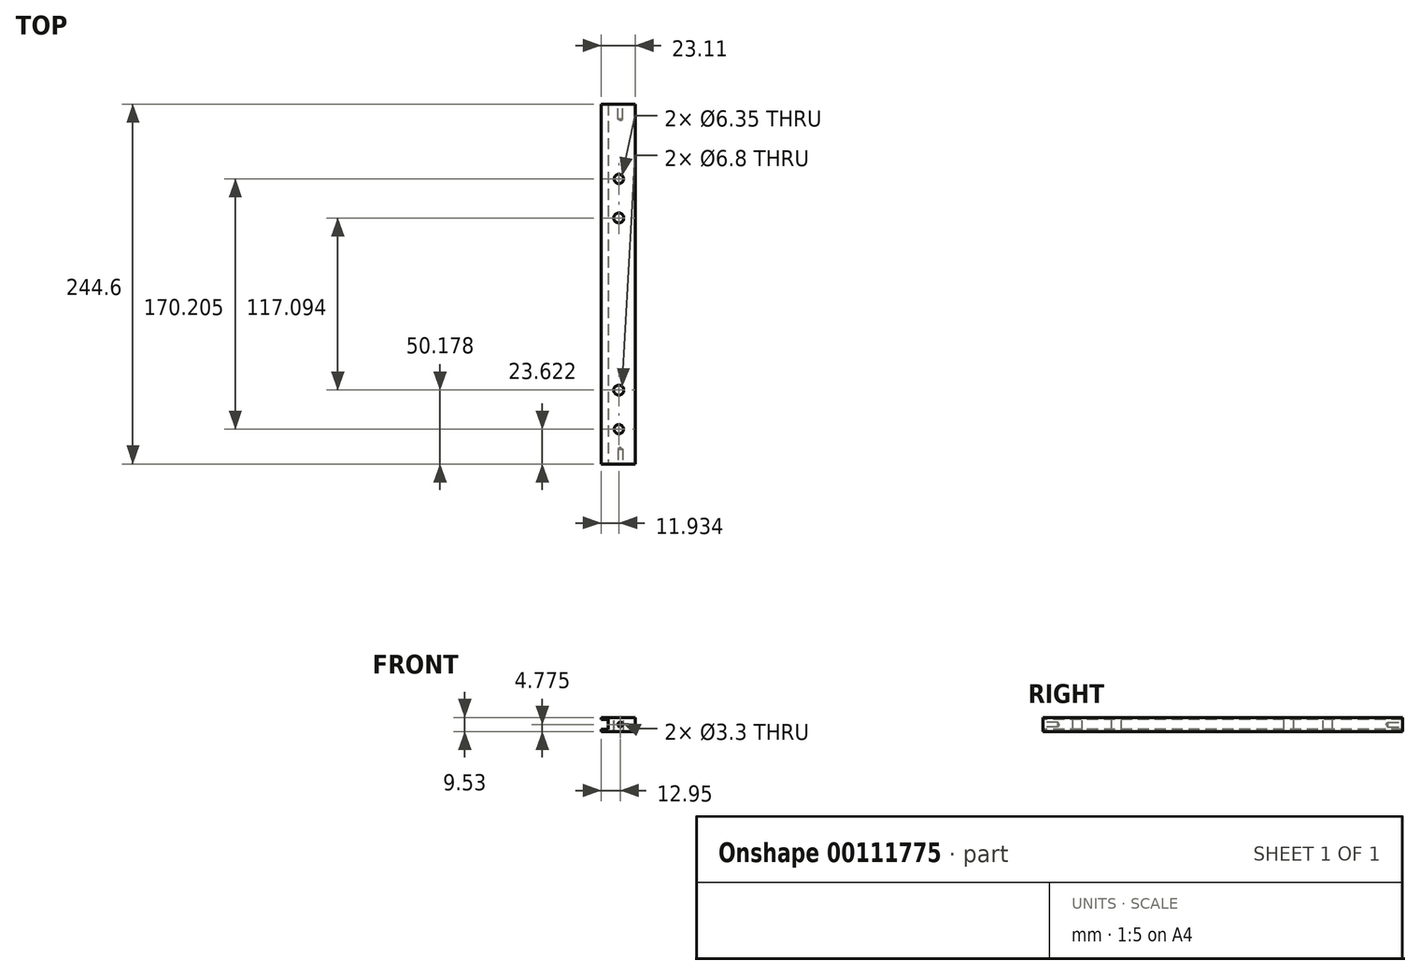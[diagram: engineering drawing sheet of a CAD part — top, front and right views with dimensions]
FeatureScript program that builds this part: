
annotation { "Feature Type Name" : "Feature", "Feature Type Description" : "" }
export const myFeature = defineFeature(function(context is Context, id is Id, definition is map)
    precondition{}
    {
        {
            var Q0;
            Q0=qCreatedBy(makeId("Top.planeOp"),FACE);
            var sketch = newSketch(context, id + "F0", { "sketchPlane" : qUnion([Q0])});
            skLineSegment(sketch, "E0.bottom", {"start": v(0, 0) * mm, "end": v(-23.11, 0) * mm});
            skLineSegment(sketch, "E0.top", {"start": v(0, 244.6) * mm, "end": v(-23.11, 244.6) * mm});
            skLineSegment(sketch, "E0.left", {"start": v(0, 0) * mm, "end": v(0, 244.6) * mm});
            skLineSegment(sketch, "E0.right", {"start": v(-23.11, 0) * mm, "end": v(-23.11, 244.6) * mm});
            skSolve(sketch);
        }
        {
            var Q0;
            Q0 = qSketchRegion(id + "F0", true);
            extrude(context, id + "F1", {"entities" : qUnion([Q0]), "depth" : 9.52 * mm});
        }
        {
            var Q0;
            Q0=makeQuery(id+"F1.opExtrude","SWEPT_FACE",FACE,{"disambiguationData":[OSD([sQuery(id+"F0.wireOp",EDGE,"E0.right")])]});
            var sketch = newSketch(context, id + "F2", { "sketchPlane" : qUnion([Q0])});
            skLineSegment(sketch, "E1.bottom", {"start": v(-244.6, 8.1) * mm, "end": v(0, 8.1) * mm});
            skLineSegment(sketch, "E1.top", {"start": v(-244.6, 1.42) * mm, "end": v(0, 1.42) * mm});
            skLineSegment(sketch, "E1.left", {"start": v(-244.6, 8.1) * mm, "end": v(-244.6, 1.42) * mm});
            skLineSegment(sketch, "E1.right", {"start": v(0, 8.1) * mm, "end": v(0, 1.42) * mm});
            skSolve(sketch);
        }
        {
            var Q0;
            Q0 = qSketchRegion(id + "F2", true);
            extrude(context, id + "F3", {"entities" : qUnion([Q0]), "operationType" : NewBodyOperationType.REMOVE, "oppositeDirection" : true, "depth" : 4.57 * mm});
        }
        {
            var Q0;
            Q0=makeQuery(id+"F1.opExtrude","CAP_FACE",FACE,{"disambiguationData":[OSD([sQuery(id+"F0.wireOp",EDGE,"E0.bottom"),sQuery(id+"F0.wireOp",EDGE,"E0.top"),sQuery(id+"F0.wireOp",EDGE,"E0.left"),sQuery(id+"F0.wireOp",EDGE,"E0.right")])],"isStart":false});
            var sketch = newSketch(context, id + "F4", { "sketchPlane" : qUnion([Q0])});
            skCircle(sketch, "E2", {"center": v(-11.18, 23.62) * mm, "radius": 3.18 * mm});
            skCircle(sketch, "E3", {"center": v(-11.18, 193.83) * mm, "radius": 3.18 * mm});
            skSolve(sketch);
        }
        {
            var Q0;
            Q0 = qSketchRegion(id + "F4", true);
            extrude(context, id + "F5", {"entities" : qUnion([Q0]), "operationType" : NewBodyOperationType.REMOVE, "endBound" : BoundingType.THROUGH_ALL, "oppositeDirection" : true, "depth" : 25.4 * mm});
        }
        {
            var Q0;
            Q0=makeQuery(id+"F1.opExtrude","SWEPT_FACE",FACE,{"disambiguationData":[OSD([sQuery(id+"F0.wireOp",EDGE,"E0.top")])]});
            var sketch = newSketch(context, id + "F6", { "sketchPlane" : qUnion([Q0])});
            skPoint(sketch, "E4", {"position": v(10.16, 4.78) * mm});
            skSolve(sketch);
        }
        {
            var Q0;
            Q0=makeQuery(id+"F1.opExtrude","SWEPT_FACE",FACE,{"disambiguationData":[OSD([sQuery(id+"F0.wireOp",EDGE,"E0.bottom")])]});
            var sketch = newSketch(context, id + "F7", { "sketchPlane" : qUnion([Q0])});
            skPoint(sketch, "E5", {"position": v(-10.16, 4.78) * mm});
            skSolve(sketch);
        }
        {
            var Q0;
            Q0=sQuery(id+"F6.wireOp",VERTEX,"E4");
            var Q1;
            Q1=makeQuery(id+"F1.opExtrude","SWEPT_BODY",BODY,{"disambiguationData":[OSD([sQuery(id+"F0.wireOp",EDGE,"E0.bottom"),sQuery(id+"F0.wireOp",EDGE,"E0.top"),sQuery(id+"F0.wireOp",EDGE,"E0.left"),sQuery(id+"F0.wireOp",EDGE,"E0.right")])]});
            hole(context, id + "F8", {"style" : HoleStyle.SIMPLE, "endStyle" : HoleEndStyle.BLIND, "standardTappedOrClearance" : lookupTablePath({ "standard" : "ISO", "engagement" : "75%", "pitch" : "0.7 mm", "size" : "M4", "type" : "Tapped" }), "standardBlindInLast" : lookupTablePath({ "standard" : "ISO", "engagement" : "75%", "pitch" : "0.7 mm", "size" : "M4", "type" : "Tapped" }), "holeDiameter" : 3.3 * mm, "holeDepth" : 10.16 * mm, "startFromSketch" : true, "locations" : qUnion([Q0]), "scope" : qUnion([Q1]), "majorDiameter" : 4 * mm});
        }
        {
            var Q0;
            Q0=sQuery(id+"F7.wireOp",VERTEX,"E5");
            var Q1;
            Q1=makeQuery(id+"F1.opExtrude","SWEPT_BODY",BODY,{"disambiguationData":[OSD([sQuery(id+"F0.wireOp",EDGE,"E0.bottom"),sQuery(id+"F0.wireOp",EDGE,"E0.top"),sQuery(id+"F0.wireOp",EDGE,"E0.left"),sQuery(id+"F0.wireOp",EDGE,"E0.right")])]});
            hole(context, id + "F9", {"style" : HoleStyle.SIMPLE, "endStyle" : HoleEndStyle.BLIND, "standardTappedOrClearance" : lookupTablePath({ "standard" : "ISO", "engagement" : "75%", "pitch" : "0.7 mm", "size" : "M4", "type" : "Tapped" }), "standardBlindInLast" : lookupTablePath({ "standard" : "ISO", "engagement" : "75%", "pitch" : "0.7 mm", "size" : "M4", "type" : "Tapped" }), "holeDiameter" : 3.3 * mm, "holeDepth" : 10.16 * mm, "startFromSketch" : true, "locations" : qUnion([Q0]), "scope" : qUnion([Q1]), "majorDiameter" : 4 * mm});
        }
        {
            var Q0;
            Q0=makeQuery(id+"F1.opExtrude","CAP_FACE",FACE,{"disambiguationData":[OSD([sQuery(id+"F0.wireOp",EDGE,"E0.bottom"),sQuery(id+"F0.wireOp",EDGE,"E0.top"),sQuery(id+"F0.wireOp",EDGE,"E0.left"),sQuery(id+"F0.wireOp",EDGE,"E0.right")])],"isStart":false});
            var sketch = newSketch(context, id + "F10", { "sketchPlane" : qUnion([Q0])});
            skPoint(sketch, "E6", {"position": v(-11.18, 50.18) * mm});
            skPoint(sketch, "E7", {"position": v(-11.18, 167.27) * mm});
            skSolve(sketch);
        }
        {
            var Q0;
            Q0=sQuery(id+"F10.wireOp",VERTEX,"E7");
            var Q1;
            Q1=sQuery(id+"F10.wireOp",VERTEX,"E6");
            var Q2;
            Q2=makeQuery(id+"F1.opExtrude","SWEPT_BODY",BODY,{"disambiguationData":[OSD([sQuery(id+"F0.wireOp",EDGE,"E0.bottom"),sQuery(id+"F0.wireOp",EDGE,"E0.top"),sQuery(id+"F0.wireOp",EDGE,"E0.left"),sQuery(id+"F0.wireOp",EDGE,"E0.right")])]});
            hole(context, id + "F11", {"style" : HoleStyle.SIMPLE, "endStyle" : HoleEndStyle.THROUGH, "standardTappedOrClearance" : lookupTablePath({ "standard" : "ISO", "engagement" : "75%", "pitch" : "1.25 mm", "size" : "M8", "type" : "Tapped" }), "standardBlindInLast" : lookupTablePath({ "standard" : "ISO", "engagement" : "75%", "pitch" : "1.25 mm", "size" : "M8", "type" : "Tapped" }), "holeDiameter" : 6.8 * mm, "startFromSketch" : true, "locations" : qUnion([Q0, Q1]), "scope" : qUnion([Q2]), "isTappedThrough" : true, "majorDiameter" : 8 * mm, "showTappedDepth" : true});
        }
    });
